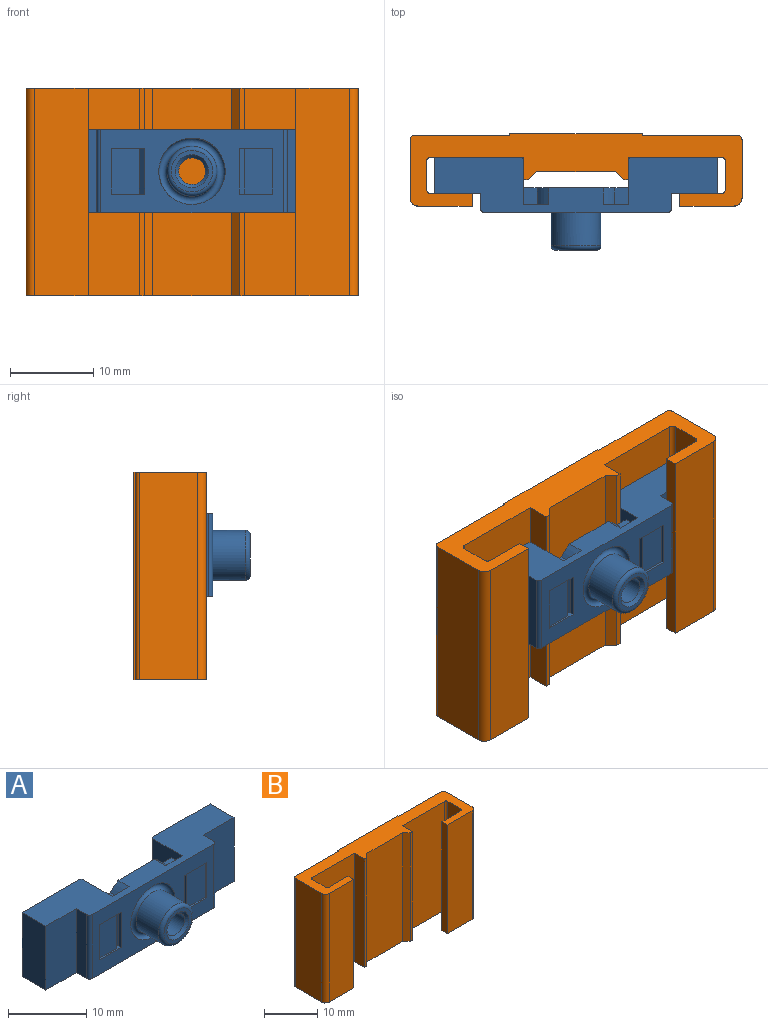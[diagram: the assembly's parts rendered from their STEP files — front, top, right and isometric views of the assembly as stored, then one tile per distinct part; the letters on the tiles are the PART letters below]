
ASSEMBLY  parts=2 mates=1
PART A: 60 faces, bbox 34x11.2x10 mm
  f0: plane 34x6.65mm, normal (0,0,-1), area 144.6mm2, adj f2,f3,f4,f6,f7,f8,f9,f10
  f1: cylinder r=6mm len=2mm, axis (0,-1,0), area 3.7mm2, adj f4,f39,f42,f59
  f2: cylinder r=6mm len=1.5mm, axis (0,-1,0), area 2.8mm2, adj f0,f4,f8,f46
  f3: cylinder r=6mm len=1.5mm, axis (0,-1,0), area 2.8mm2, adj f0,f4,f7,f43
  f4: plane 12.7x10mm, normal (0,1,0), area 75.3mm2, adj f0,f1,f2,f3,f13,f14,f23,f27
  f5: plane 3.03x1.25mm, normal (0,1,0), area 2.8mm2, adj f14,f23,f47,f59
  f6: plane 10x1.85mm, normal (-1,0,0), area 18.5mm2, adj f0,f12,f19,f59
  f7: plane 3.03x1.25mm, normal (0,1,0), area 2.8mm2, adj f0,f3,f14,f43
  f8: plane 3.04x1.25mm, normal (0,1,0), area 2.9mm2, adj f0,f2,f13,f46
  f9: plane 10x1.85mm, normal (1,0,0), area 18.5mm2, adj f0,f10,f15,f59
  f10: cylinder r=0.5mm len=10mm, axis (0,0,1), area 7.9mm2, adj f0,f9,f11,f59
  f11: plane 22x10mm, normal (0,-1,0), area 125.7mm2, adj f0,f10,f12,f26,f35,f41,f48,f50
  f12: cylinder r=0.5mm len=10mm, axis (0,0,1), area 7.9mm2, adj f0,f6,f11,f59
  f13: plane 10x5.4mm, normal (1,0,0), area 41.9mm2, adj f0,f4,f8,f16,f34,f38,f39,f42
  f14: plane 10x5.4mm, normal (-1,0,0), area 41.9mm2, adj f0,f4,f5,f7,f22,f36,f37,f40
  f15: plane 10x5.5mm, normal (0,-1,0), area 55mm2, adj f0,f9,f20,f59
  f16: plane 10x0.25mm, normal (0.71,0.71,0), area 3.5mm2, adj f0,f13,f17,f59
  f17: plane 10.4x10mm, normal (0,1,0), area 104mm2, adj f0,f16,f18,f59
  f18: plane 10x4.3mm, normal (-1,0,0), area 43mm2, adj f0,f17,f19,f59
  f19: plane 10x5.5mm, normal (0,-1,0), area 55mm2, adj f0,f6,f18,f59
  f20: plane 10x4.3mm, normal (1,0,0), area 43mm2, adj f0,f15,f21,f59
  f21: plane 10.4x10mm, normal (0,1,0), area 104mm2, adj f0,f20,f22,f59
  f22: plane 10x0.25mm, normal (-0.71,0.71,0), area 3.5mm2, adj f0,f14,f21,f59
  f23: cylinder r=6mm len=2mm, axis (0,-1,0), area 3.7mm2, adj f4,f5,f47,f59
  f24: torus R=2.5mm, axis (0,-1,0), area 13.9mm2, adj f25,f44
  f25: cylinder r=3mm len=6mm, axis (0,-1,0), area 75.4mm2, adj f24,f26
  f26: torus R=3.5mm, axis (0,-1,0), area 34.5mm2, adj f11,f25
  f27: cylinder r=3.25mm len=6.5mm, axis (0,-1,0), area 10.2mm2, adj f4,f28
  f28: torus R=2.75mm, axis (0,-1,0), area 15.1mm2, adj f27,f45
  f29: cone r=1.8mm half-angle=45deg, axis (0,1,0), area 6.4mm2, adj f30,f45
  f30: cylinder r=1.6mm len=5.7mm, axis (0,-1,0), area 57.3mm2, adj f29,f31
  f31: cone r=1.8mm half-angle=45deg, axis (0,-1,0), area 6.4mm2, adj f30,f44
  f32: plane 5.5x0.65mm, normal (-0.71,-0.71,0), area 5.1mm2, adj f35,f48,f53,f55
  f33: plane 5.5x0.65mm, normal (0.71,-0.71,0), area 5.1mm2, adj f41,f50,f54,f56
  f34: plane 0.65x0.65mm, normal (0,0,-1), area 0.2mm2, adj f4,f13,f49
  f35: plane 4x1.15mm, normal (0,0,-1), area 1.4mm2, adj f11,f32,f48,f52,f55,f58
  f36: plane 0.65x0.65mm, normal (0,0,-1), area 0.2mm2, adj f4,f14,f37
  f37: plane 5.5x0.65mm, normal (0.71,0.71,0), area 5.1mm2, adj f4,f14,f36,f40
  f38: plane 0.65x0.65mm, normal (0,0,1), area 0.2mm2, adj f4,f13,f49
  f39: plane 2x1.67mm, normal (0,0,1), area 3.3mm2, adj f1,f4,f13,f42
  f40: plane 0.65x0.65mm, normal (0,0,1), area 0.2mm2, adj f4,f14,f37
  f41: plane 4x1.15mm, normal (0,0,1), area 1.4mm2, adj f11,f33,f50,f51,f56,f57
  f42: plane 3.04x1.25mm, normal (0,1,0), area 2.9mm2, adj f1,f13,f39,f59
  f43: plane 1.66x1.5mm, normal (0,0,-1), area 2.5mm2, adj f3,f4,f7,f14
  f44: plane 5x5mm, normal (0,-1,0), area 7.1mm2, adj f24,f31
  f45: plane 5.5x5.5mm, normal (0,1,0), area 11.2mm2, adj f28,f29
  f46: plane 1.67x1.5mm, normal (0,0,-1), area 2.5mm2, adj f2,f4,f8,f13
  f47: plane 2x1.66mm, normal (0,0,1), area 3.3mm2, adj f4,f5,f14,f23
  f48: plane 5.5x0.5mm, normal (-1,0,0), area 2.8mm2, adj f11,f32,f35,f53
  f49: plane 5.5x0.65mm, normal (-0.71,0.71,0), area 5.1mm2, adj f4,f13,f34,f38
  f50: plane 5.5x0.5mm, normal (1,0,0), area 2.8mm2, adj f11,f33,f41,f54
  f51: plane 5.5x0.25mm, normal (-1,0,0), area 1.4mm2, adj f11,f41,f54,f57
  f52: plane 5.5x0.25mm, normal (1,0,0), area 1.4mm2, adj f11,f35,f53,f58
  f53: plane 4x1.15mm, normal (0,0,1), area 1.4mm2, adj f11,f32,f48,f52,f55,f58
  f54: plane 4x1.15mm, normal (0,0,-1), area 1.4mm2, adj f11,f33,f50,f51,f56,f57
  f55: plane 5.5x0.9mm, normal (1,0,0), area 4.9mm2, adj f32,f35,f53,f58
  f56: plane 5.5x0.9mm, normal (-1,0,0), area 4.9mm2, adj f33,f41,f54,f57
  f57: plane 5.5x3.35mm, normal (0,-1,0), area 18.4mm2, adj f41,f51,f54,f56
  f58: plane 5.5x3.35mm, normal (0,-1,0), area 18.4mm2, adj f35,f52,f53,f55
  f59: plane 34x6.65mm, normal (0,0,1), area 141.6mm2, adj f1,f4,f5,f6,f9,f10,f11,f12
PART B: 34 faces, bbox 40x8.7x25 mm
  f0: plane 25x0.2mm, normal (1,0,0), area 5mm2, adj f1,f31,f32,f33
  f1: plane 25x11.5mm, normal (0,1,0), area 287.5mm2, adj f0,f2,f32,f33
  f2: cylinder r=0.5mm len=25mm, axis (0,0,1), area 19.6mm2, adj f1,f3,f32,f33
  f3: plane 25x7mm, normal (1,0,0), area 175mm2, adj f2,f4,f32,f33
  f4: cylinder r=1mm len=25mm, axis (0,0,1), area 39.3mm2, adj f3,f5,f32,f33
  f5: plane 25x6.5mm, normal (0,-1,0), area 162.5mm2, adj f4,f6,f32,f33
  f6: plane 25x1.5mm, normal (-1,0,0), area 37.5mm2, adj f5,f7,f32,f33
  f7: plane 25x5mm, normal (0,1,0), area 125mm2, adj f6,f8,f32,f33
  f8: cylinder r=0.5mm len=25mm, axis (0,0,1), area 19.6mm2, adj f7,f9,f32,f33
  f9: plane 25x3.4mm, normal (-1,0,0), area 85mm2, adj f8,f10,f32,f33
  f10: cylinder r=0.5mm len=25mm, axis (0,0,1), area 19.6mm2, adj f9,f11,f32,f33
  f11: plane 25x11.2mm, normal (0,-1,0), area 280mm2, adj f10,f12,f32,f33
  f12: plane 25x2.7mm, normal (1,0,0), area 67.5mm2, adj f11,f13,f32,f33
  f13: plane 25x0.55mm, normal (0,-1,0), area 13.8mm2, adj f12,f14,f32,f33
  f14: plane 25x1mm, normal (-0.71,-0.71,0), area 35.4mm2, adj f13,f15,f32,f33
  f15: plane 25x9.5mm, normal (0,-1,0), area 237.5mm2, adj f14,f16,f32,f33
  f16: plane 25x1mm, normal (0.71,-0.71,0), area 35.4mm2, adj f15,f17,f32,f33
  f17: plane 25x0.55mm, normal (0,-1,0), area 13.8mm2, adj f16,f18,f32,f33
  f18: plane 25x2.7mm, normal (-1,0,0), area 67.5mm2, adj f17,f19,f32,f33
  f19: plane 25x11.2mm, normal (0,-1,0), area 280mm2, adj f18,f20,f32,f33
  f20: cylinder r=0.5mm len=25mm, axis (0,0,1), area 19.6mm2, adj f19,f21,f32,f33
  f21: plane 25x3.4mm, normal (1,0,0), area 85mm2, adj f20,f22,f32,f33
  f22: cylinder r=0.5mm len=25mm, axis (0,0,1), area 19.6mm2, adj f21,f23,f32,f33
  f23: plane 25x5mm, normal (0,1,0), area 125mm2, adj f22,f24,f32,f33
  f24: plane 25x1.5mm, normal (1,0,0), area 37.5mm2, adj f23,f25,f32,f33
  f25: plane 25x6.5mm, normal (0,-1,0), area 162.5mm2, adj f24,f26,f32,f33
  f26: cylinder r=1mm len=25mm, axis (0,0,1), area 39.3mm2, adj f25,f27,f32,f33
  f27: plane 25x7mm, normal (-1,0,0), area 175mm2, adj f26,f28,f32,f33
  f28: cylinder r=0.5mm len=25mm, axis (0,0,1), area 19.6mm2, adj f27,f29,f32,f33
  f29: plane 25x11.5mm, normal (0,1,0), area 287.5mm2, adj f28,f30,f32,f33
  f30: plane 25x0.2mm, normal (-1,0,0), area 5mm2, adj f29,f31,f32,f33
  f31: plane 25x16mm, normal (0,1,0), area 400mm2, adj f0,f30,f32,f33
  f32: plane 40x8.7mm, normal (0,0,-1), area 170.5mm2, adj f0,f1,f2,f3,f4,f5,f6,f7
  f33: plane 40x8.7mm, normal (0,0,1), area 170.5mm2, adj f0,f1,f2,f3,f4,f5,f6,f7
PLACE A t=(0,0,5)mm
PLACE B at identity fixed
MATE slider B.f33 <-> A.f59  axis (0,0,1) through (-18,-5,25)mm
